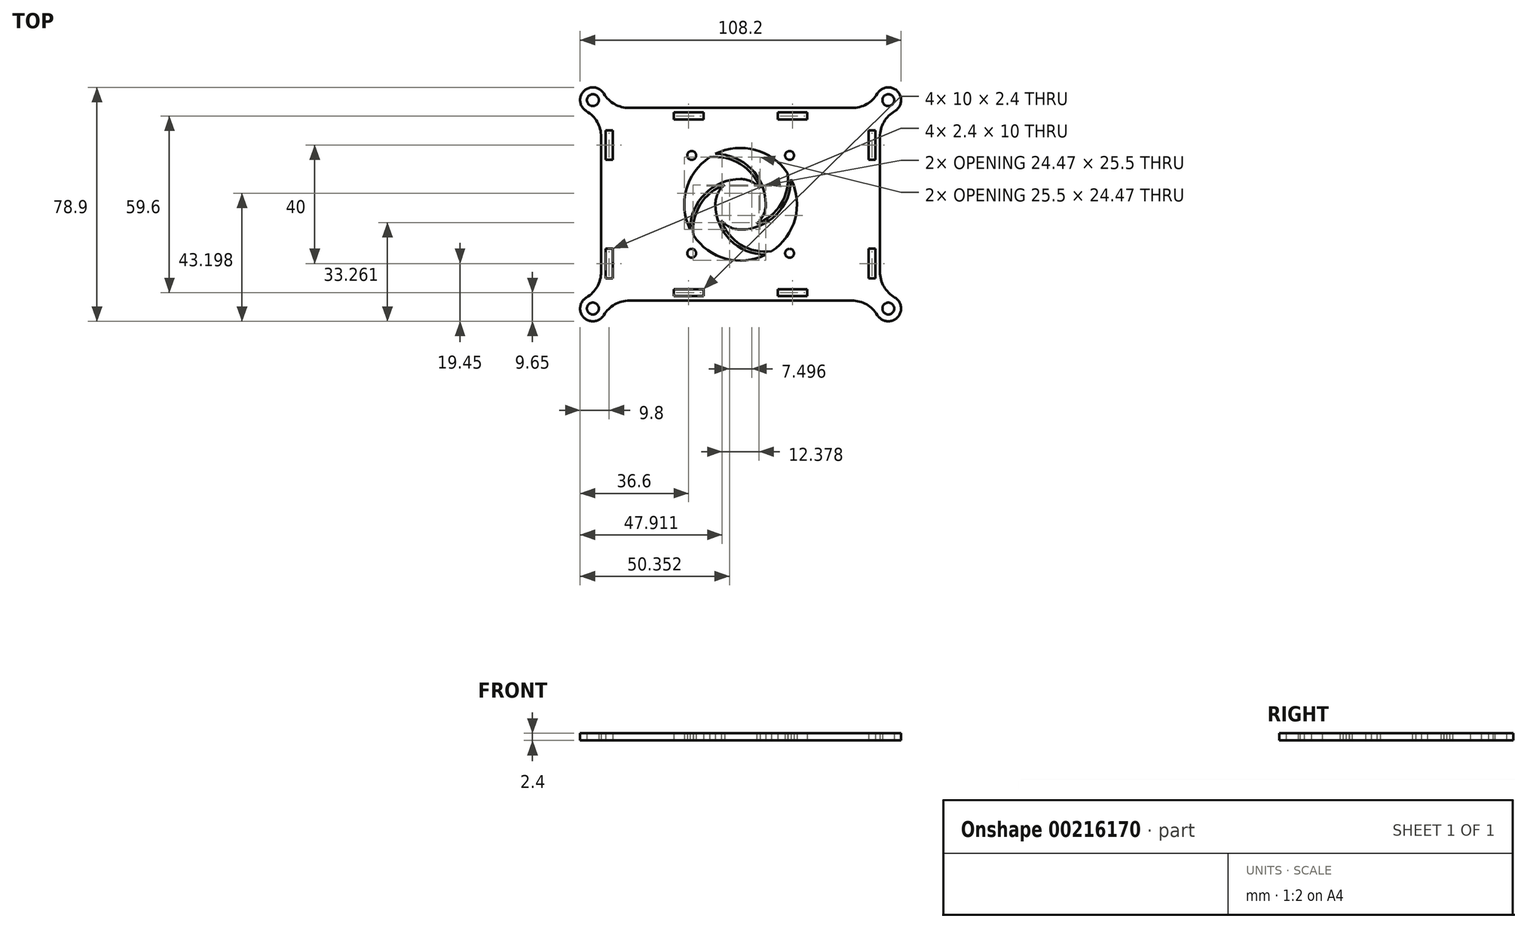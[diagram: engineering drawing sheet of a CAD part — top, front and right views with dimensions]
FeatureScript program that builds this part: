
annotation { "Feature Type Name" : "Feature", "Feature Type Description" : "" }
export const myFeature = defineFeature(function(context is Context, id is Id, definition is map)
    precondition{}
    {
        {
            var Q0;
            Q0=qCreatedBy(makeId("Top.planeOp"),FACE);
            var sketch = newSketch(context, id + "F0", { "sketchPlane" : qUnion([Q0])});
            skLineSegment(sketch, "E0.bottom", {"start": v(37.53, 32.5) * mm, "end": v(-37.53, 32.5) * mm});
            skLineSegment(sketch, "E0.top", {"start": v(37.53, -32.5) * mm, "end": v(-37.53, -32.5) * mm});
            skLineSegment(sketch, "E0.left", {"start": v(47, 22.8) * mm, "end": v(47, -22.8) * mm});
            skLineSegment(sketch, "E0.right", {"start": v(-47, 22.8) * mm, "end": v(-47, 0) * mm});
            skCircle(sketch, "E1", {"center": v(-49.8, 35.15) * mm, "radius": 2 * mm});
            skArc(sketch, "E2", {"start": v(-46.11, 37.36) * mm, "mid": v(-52.86, 38.17) * mm, "end": v(-51.97, 31.43) * mm});
            skCircle(sketch, "E3", {"center": v(49.8, 35.15) * mm, "radius": 2 * mm});
            skArc(sketch, "E4", {"start": v(51.97, 31.43) * mm, "mid": v(52.86, 38.17) * mm, "end": v(46.11, 37.36) * mm});
            skCircle(sketch, "E5", {"center": v(49.8, -35.15) * mm, "radius": 2 * mm});
            skArc(sketch, "E6", {"start": v(46.11, -37.36) * mm, "mid": v(52.86, -38.17) * mm, "end": v(51.97, -31.43) * mm});
            skCircle(sketch, "E7", {"center": v(-49.8, -35.15) * mm, "radius": 2 * mm});
            skArc(sketch, "E8", {"start": v(-51.97, -31.43) * mm, "mid": v(-52.86, -38.17) * mm, "end": v(-46.11, -37.36) * mm});
            skPoint(sketch, "E9.orphan", {"position": v(-47, 32.5) * mm});
            skPoint(sketch, "E10.visualSharp", {"position": v(-46.41, 32.5) * mm});
            skArc(sketch, "E10.filletArc", {"start": v(-46.11, 37.36) * mm, "mid": v(-42.46, 33.8) * mm, "end": v(-37.53, 32.5) * mm});
            skPoint(sketch, "E11.visualSharp", {"position": v(-47, 31.89) * mm});
            skArc(sketch, "E11.filletArc", {"start": v(-47, 22.8) * mm, "mid": v(-48.33, 27.78) * mm, "end": v(-51.97, 31.43) * mm});
            skPoint(sketch, "E12.orphan", {"position": v(47, 32.5) * mm});
            skPoint(sketch, "E13.orphan", {"position": v(47, -32.5) * mm});
            skPoint(sketch, "E14.orphan", {"position": v(-47, -32.5) * mm});
            skPoint(sketch, "E15.visualSharp", {"position": v(-46.41, -32.5) * mm});
            skArc(sketch, "E15.filletArc", {"start": v(-37.53, -32.5) * mm, "mid": v(-42.46, -33.8) * mm, "end": v(-46.11, -37.36) * mm});
            skPoint(sketch, "E16.visualSharp", {"position": v(-47, -31.89) * mm});
            skArc(sketch, "E16.filletArc", {"start": v(-51.97, -31.43) * mm, "mid": v(-48.33, -27.78) * mm, "end": v(-47, -22.8) * mm});
            skPoint(sketch, "E17.visualSharp", {"position": v(46.41, -32.5) * mm});
            skArc(sketch, "E17.filletArc", {"start": v(46.11, -37.36) * mm, "mid": v(42.46, -33.8) * mm, "end": v(37.53, -32.5) * mm});
            skPoint(sketch, "E18.visualSharp", {"position": v(47, -31.89) * mm});
            skArc(sketch, "E18.filletArc", {"start": v(47, -22.8) * mm, "mid": v(48.33, -27.78) * mm, "end": v(51.97, -31.43) * mm});
            skPoint(sketch, "E19.visualSharp", {"position": v(47, 31.89) * mm});
            skArc(sketch, "E19.filletArc", {"start": v(51.97, 31.43) * mm, "mid": v(48.33, 27.78) * mm, "end": v(47, 22.8) * mm});
            skPoint(sketch, "E20.visualSharp", {"position": v(46.41, 32.5) * mm});
            skArc(sketch, "E20.filletArc", {"start": v(37.53, 32.5) * mm, "mid": v(42.46, 33.8) * mm, "end": v(46.11, 37.36) * mm});
            skPoint(sketch, "E21.middle", {"position": v(-47, 0) * mm});
            skPoint(sketch, "E22.orphan", {"position": v(-53, -7.5) * mm});
            skLineSegment(sketch, "E23.trimOffspring", {"start": v(-47, 0) * mm, "end": v(-47, -22.8) * mm});
            skLineSegment(sketch, "E24.bottom", {"start": v(-22.5, 31) * mm, "end": v(-12.5, 31) * mm});
            skLineSegment(sketch, "E24.top", {"start": v(-22.5, 28.6) * mm, "end": v(-12.5, 28.6) * mm});
            skLineSegment(sketch, "E24.left", {"start": v(-22.5, 31) * mm, "end": v(-22.5, 28.6) * mm});
            skLineSegment(sketch, "E24.right", {"start": v(-12.5, 31) * mm, "end": v(-12.5, 28.6) * mm});
            skLineSegment(sketch, "E25.bottom", {"start": v(12.5, 31) * mm, "end": v(22.5, 31) * mm});
            skLineSegment(sketch, "E25.top", {"start": v(12.5, 28.6) * mm, "end": v(22.5, 28.6) * mm});
            skLineSegment(sketch, "E25.left", {"start": v(12.5, 31) * mm, "end": v(12.5, 28.6) * mm});
            skLineSegment(sketch, "E25.right", {"start": v(22.5, 31) * mm, "end": v(22.5, 28.6) * mm});
            skLineSegment(sketch, "E26.bottom", {"start": v(43.1, 25) * mm, "end": v(45.5, 25) * mm});
            skLineSegment(sketch, "E26.top", {"start": v(43.1, 15) * mm, "end": v(45.5, 15) * mm});
            skLineSegment(sketch, "E26.left", {"start": v(43.1, 25) * mm, "end": v(43.1, 15) * mm});
            skLineSegment(sketch, "E26.right", {"start": v(45.5, 25) * mm, "end": v(45.5, 15) * mm});
            skLineSegment(sketch, "E27.bottom", {"start": v(43.1, -15) * mm, "end": v(45.5, -15) * mm});
            skLineSegment(sketch, "E27.top", {"start": v(43.1, -25) * mm, "end": v(45.5, -25) * mm});
            skLineSegment(sketch, "E27.left", {"start": v(43.1, -15) * mm, "end": v(43.1, -25) * mm});
            skLineSegment(sketch, "E27.right", {"start": v(45.5, -15) * mm, "end": v(45.5, -25) * mm});
            skLineSegment(sketch, "E28.bottom", {"start": v(12.5, -28.6) * mm, "end": v(22.5, -28.6) * mm});
            skLineSegment(sketch, "E28.top", {"start": v(12.5, -31) * mm, "end": v(22.5, -31) * mm});
            skLineSegment(sketch, "E28.left", {"start": v(12.5, -28.6) * mm, "end": v(12.5, -31) * mm});
            skLineSegment(sketch, "E28.right", {"start": v(22.5, -28.6) * mm, "end": v(22.5, -31) * mm});
            skLineSegment(sketch, "E29.bottom", {"start": v(-22.5, -28.6) * mm, "end": v(-12.5, -28.6) * mm});
            skLineSegment(sketch, "E29.top", {"start": v(-22.5, -31) * mm, "end": v(-12.5, -31) * mm});
            skLineSegment(sketch, "E29.left", {"start": v(-22.5, -28.6) * mm, "end": v(-22.5, -31) * mm});
            skLineSegment(sketch, "E29.right", {"start": v(-12.5, -28.6) * mm, "end": v(-12.5, -31) * mm});
            skLineSegment(sketch, "E30.bottom", {"start": v(-45.5, 25) * mm, "end": v(-43.1, 25) * mm});
            skLineSegment(sketch, "E30.top", {"start": v(-45.5, 15) * mm, "end": v(-43.1, 15) * mm});
            skLineSegment(sketch, "E30.left", {"start": v(-45.5, 25) * mm, "end": v(-45.5, 15) * mm});
            skLineSegment(sketch, "E30.right", {"start": v(-43.1, 25) * mm, "end": v(-43.1, 15) * mm});
            skPoint(sketch, "E31.oppositeSnap0", {"position": v(-43.1, 20) * mm});
            skLineSegment(sketch, "E31.bottom", {"start": v(-45.5, -15) * mm, "end": v(-43.1, -15) * mm});
            skLineSegment(sketch, "E31.top", {"start": v(-45.5, -25) * mm, "end": v(-43.1, -25) * mm});
            skLineSegment(sketch, "E31.left", {"start": v(-45.5, -15) * mm, "end": v(-45.5, -25) * mm});
            skLineSegment(sketch, "E31.right", {"start": v(-43.1, -15) * mm, "end": v(-43.1, -25) * mm});
            skArc(sketch, "E32", {"start": v(6.56, 5.4) * mm, "mid": v(3.63, 7.69) * mm, "end": v(0, 8.5) * mm});
            skArc(sketch, "E33", {"start": v(15.88, 10.43) * mm, "mid": v(4.95, 18.34) * mm, "end": v(-8.49, 17) * mm});
            skArc(sketch, "E34", {"start": v(0, -8.5) * mm, "mid": v(12.02, -3.53) * mm, "end": v(17, 8.49) * mm});
            skArc(sketch, "E35", {"start": v(5.4, -6.56) * mm, "mid": v(13.62, 0.1) * mm, "end": v(15.88, 10.43) * mm});
            skArc(sketch, "E36", {"start": v(8.5, 0) * mm, "mid": v(3.53, 12.02) * mm, "end": v(-8.49, 17) * mm});
            skArc(sketch, "E37", {"start": v(6.56, 5.4) * mm, "mid": v(-0.1, 13.62) * mm, "end": v(-10.43, 15.88) * mm});
            skArc(sketch, "E38", {"start": v(0, 8.5) * mm, "mid": v(-12.02, 3.53) * mm, "end": v(-17, -8.49) * mm});
            skArc(sketch, "E39", {"start": v(-5.4, 6.56) * mm, "mid": v(-13.62, -0.1) * mm, "end": v(-15.88, -10.43) * mm});
            skArc(sketch, "E40", {"start": v(-8.5, 0) * mm, "mid": v(-3.53, -12.02) * mm, "end": v(8.49, -17) * mm});
            skArc(sketch, "E41", {"start": v(-6.56, -5.4) * mm, "mid": v(0.1, -13.62) * mm, "end": v(10.43, -15.88) * mm});
            skPoint(sketch, "E42.orphan", {"position": v(7.5, 0) * mm});
            skPoint(sketch, "E43.orphan", {"position": v(0, -7.5) * mm});
            skArc(sketch, "E44.trimOffspring", {"start": v(5.4, -6.56) * mm, "mid": v(7.69, -3.63) * mm, "end": v(8.5, 0) * mm});
            skPoint(sketch, "E45.orphan", {"position": v(0, 7.5) * mm});
            skArc(sketch, "E46.trimOffspring", {"start": v(-5.4, 6.56) * mm, "mid": v(-7.69, 3.63) * mm, "end": v(-8.5, 0) * mm});
            skPoint(sketch, "E47.orphan", {"position": v(-7.5, 0) * mm});
            skArc(sketch, "E48.trimOffspring", {"start": v(-6.56, -5.4) * mm, "mid": v(-3.63, -7.69) * mm, "end": v(0, -8.5) * mm});
            skArc(sketch, "E49.trimOffspring", {"start": v(-15.88, -10.43) * mm, "mid": v(-4.95, -18.34) * mm, "end": v(8.49, -17) * mm});
            skArc(sketch, "E50.trimOffspring", {"start": v(-10.43, 15.88) * mm, "mid": v(-18.34, 4.95) * mm, "end": v(-17, -8.49) * mm});
            skArc(sketch, "E51.trimOffspring", {"start": v(10.43, -15.88) * mm, "mid": v(18.34, -4.95) * mm, "end": v(17, 8.49) * mm});
            skCircle(sketch, "E52", {"center": v(-16.5, 16.5) * mm, "radius": 1.5 * mm});
            skCircle(sketch, "E53", {"center": v(16.5, 16.5) * mm, "radius": 1.5 * mm});
            skCircle(sketch, "E54", {"center": v(-16.49, -16.5) * mm, "radius": 1.5 * mm});
            skCircle(sketch, "E55", {"center": v(16.51, -16.5) * mm, "radius": 1.5 * mm});
            skSolve(sketch);
        }
        {
            var Q0;
            Q0=qSketchRegion(id+"F0",true);
            extrude(context, id + "F1", {"entities" : qUnion([Q0]), "depth" : 2.4 * mm});
        }
    });
